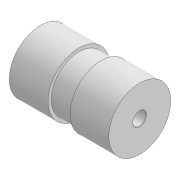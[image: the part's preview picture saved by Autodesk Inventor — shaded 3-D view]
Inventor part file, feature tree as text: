
AUTODESK INVENTOR PART (.ipt)
format: ipt  version: 2022 (Build 260153000, 153)  size: 120,320 bytes
history: native  units: mm
features: other x5, sketch x3, extrude x2, hole x1, fillet x1
ambient origin geometry x8: Origin, YZ Plane, XZ Plane, XY Plane, X Axis, Y Axis, Z Axis, Center Point
bodies: Body1 (feature_tree)
feature tree (12):
  other  "Твердое тело1"
  extrude  "Выдавливание1"  Depth=28.0mm
  hole  "Отверстие1"  [1 undecoded]
  fillet  "Сопряжение1"  Radius=0.2mm
  other  "РабПлоскость2"
  extrude  "Выдавливание3"  Depth=20.0mm
  sketch  "Эскиз1"
  sketch  "Эскиз2"
  sketch  "Эскиз4"
  other  "<userpath>\Documents\Inventor\Файлы Inventor\Конвейр без шпилек сборка.iam"
  other  "Конвейр без шпилек сборка.iam"
  other  "Стенка конвейера:1"
note: 1 required parameter value undecoded (feature->parameter linkage not recoverable at this tier; creation-order binding heuristic only, values carry confidence <= 0.55)
